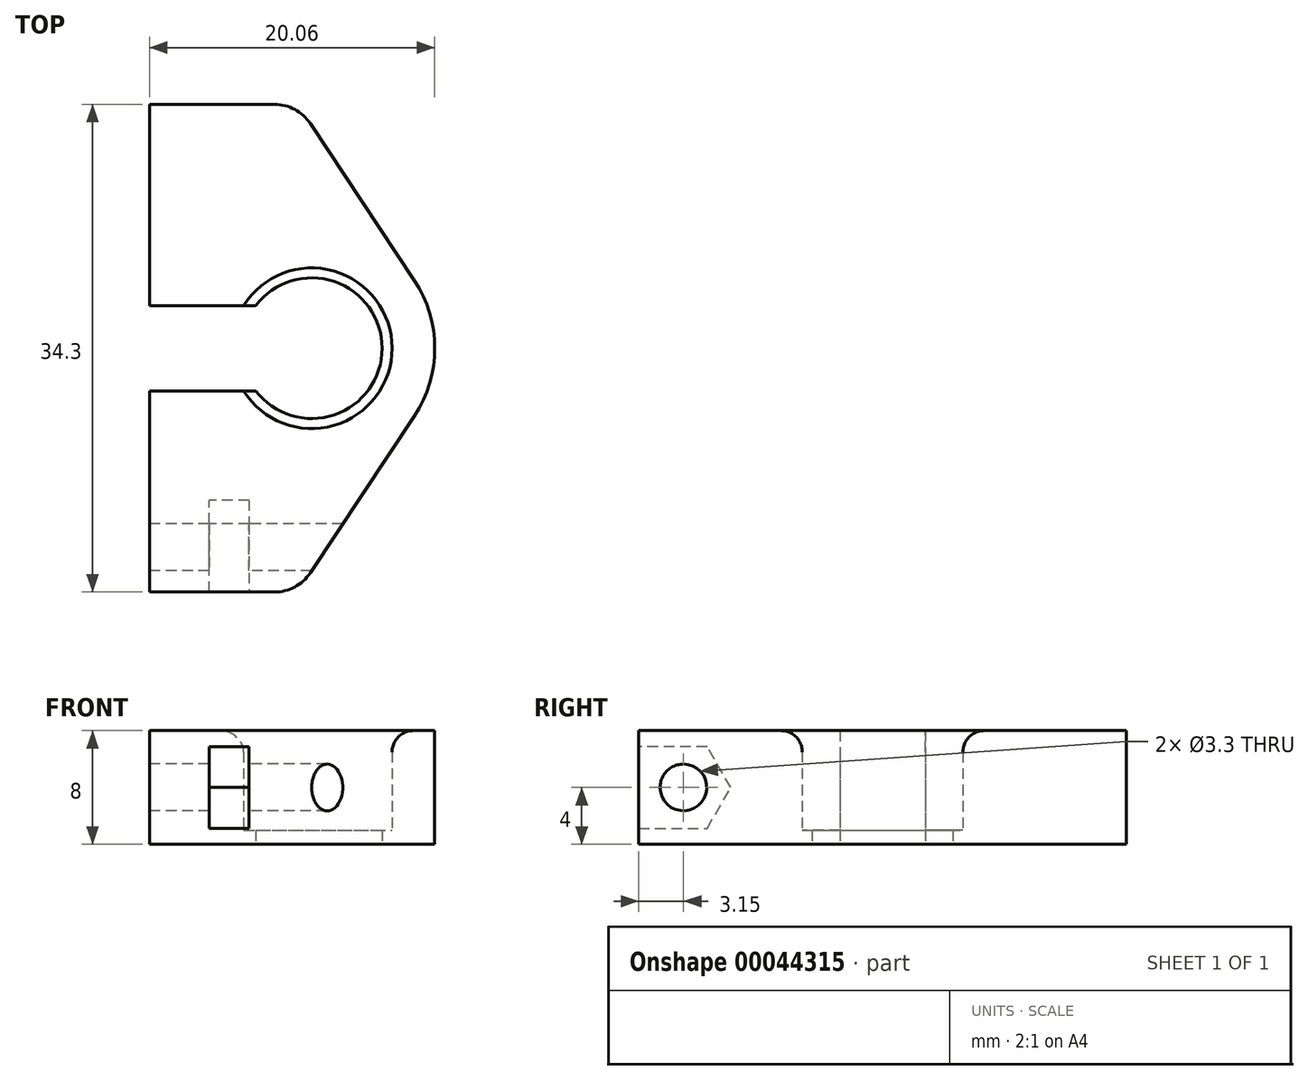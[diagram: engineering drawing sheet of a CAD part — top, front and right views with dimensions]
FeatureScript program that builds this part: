
annotation { "Feature Type Name" : "Feature", "Feature Type Description" : "" }
export const myFeature = defineFeature(function(context is Context, id is Id, definition is map)
    precondition{}
    {
        {
            assignVariable(context, id + "F0", {"name" : "Toleranz", "anyValue" : 0.3});
        }
        {
            assignVariable(context, id + "F1", {"name" : "BearingHeight", "anyValue" : 8});
        }
        {
            var Q0;
            Q0=qCreatedBy(makeId("Top.planeOp"),FACE);
            var sketch = newSketch(context, id + "F2", { "sketchPlane" : qUnion([Q0])});
            skCircle(sketch, "E0", {"center": v(0, 0) * mm, "radius": 2.65 * mm});
            skCircle(sketch, "E1", {"center": v(0, 0) * mm, "radius": 5.65 * mm});
            skCircle(sketch, "E2", {"center": v(0, 0) * mm, "radius": 8.65 * mm});
            skPoint(sketch, "E3", {"position": v(-11.4, 0) * mm});
            skLineSegment(sketch, "E4", {"start": v(-11.4, 3) * mm, "end": v(-11.4, -3) * mm, "construction": true});
            skLineSegment(sketch, "E5", {"start": v(-11.4, -17.15) * mm, "end": v(-1, -17.15) * mm});
            skLineSegment(sketch, "E6", {"start": v(-1, -17.15) * mm, "end": v(7.2, -4.78) * mm});
            skLineSegment(sketch, "E7", {"start": v(-11.4, 0) * mm, "end": v(-11.4, -17.15) * mm});
            skLineSegment(sketch, "E8", {"start": v(-28.2, 0) * mm, "end": v(26.8, 0) * mm, "construction": true});
            skLineSegment(sketch, "E9.MirrorCS", {"start": v(-1, 17.15) * mm, "end": v(7.2, 4.78) * mm});
            skLineSegment(sketch, "E10.MirrorCS", {"start": v(-11.4, 17.15) * mm, "end": v(-1, 17.15) * mm});
            skLineSegment(sketch, "E11.MirrorCS", {"start": v(-11.4, 0) * mm, "end": v(-11.41, 17.15) * mm});
            skCircle(sketch, "E12", {"center": v(0, 0) * mm, "radius": 4.95 * mm});
            skLineSegment(sketch, "E13", {"start": v(-11.4, -3) * mm, "end": v(-3.94, -3) * mm});
            skLineSegment(sketch, "E14.MirrorCS", {"start": v(-11.4, 3) * mm, "end": v(-3.94, 3) * mm});
            skSolve(sketch);
        }
        {
            var Q0;
            {var subQ2=sQuery(id+"F2.wireOp",EDGE,"3LThoHS6-l1Lm-BIrZ-PV6s-VWp7ep7WF0tf");Q0=makeQuery(id+"F2.imprint","IMPRINT",FACE,{"disambiguationData":[TD([[makeQuery(id+"F2.imprint","IMPRINT",EDGE,{"derivedFrom":subQ2}),-1.0]])]});}
            var Q1;
            {var subQ2=sQuery(id+"F2.wireOp",EDGE,"E9.MirrorCS");Q1=makeQuery(id+"F2.imprint","IMPRINT",FACE,{"disambiguationData":[TD([[makeQuery(id+"F2.imprint","IMPRINT",EDGE,{"derivedFrom":subQ2}),-1.0]])]});}
            var Q2;
            {var subQ1=sQuery(id+"F2.wireOp",EDGE,"E5");Q2=makeQuery(id+"F2.imprint","IMPRINT",FACE,{"disambiguationData":[TD([[makeQuery(id+"F2.imprint","IMPRINT",EDGE,{"derivedFrom":subQ1}),1.0]])]});}
            var Q3;
            {var subQ3=sQuery(id+"F2.wireOp",EDGE,"E13");var subQ7=sQuery(id+"F2.wireOp",EDGE,"E1");var subQ8=makeQuery(id+"F2.imprint","INTERSECT",VERTEX,{"derivedFrom":[subQ7,subQ3]});Q3=makeQuery(id+"F2.imprint","IMPRINT",FACE,{"disambiguationData":[TD([[makeQuery(id+"F2.imprint","IMPRINT",EDGE,{"disambiguationData":[TD([[subQ8,-1.0]])],"derivedFrom":subQ7}),-1.0]])]});}
            extrude(context, id + "F3", {"entities" : qUnion([Q0, Q1, Q2, Q3]), "depth" : (getVariable(context, 'BearingHeight')) * mm});
        }
        {
            var Q0;
            {var subQ0=sQuery(id+"F2.wireOp",EDGE,"E13");var subQ1=sQuery(id+"F2.wireOp",EDGE,"E1");var subQ2=makeQuery(id+"F2.imprint","INTERSECT",VERTEX,{"derivedFrom":[subQ1,subQ0]});Q0=makeQuery(id+"F2.imprint","IMPRINT",FACE,{"disambiguationData":[TD([[makeQuery(id+"F2.imprint","IMPRINT",EDGE,{"disambiguationData":[TD([[subQ2,-1.0]])],"derivedFrom":subQ1}),1.0]])]});}
            extrude(context, id + "F4", {"entities" : qUnion([Q0]), "operationType" : NewBodyOperationType.ADD, "depth" : 1 * mm});
        }
        {
            var Q0;
            Q0=makeQuery(id+"F3.opExtrude","SWEPT_FACE",FACE,{"disambiguationData":[OSD([sQuery(id+"F2.wireOp",EDGE,"E7")])]});
            var sketch = newSketch(context, id + "F5", { "sketchPlane" : qUnion([Q0])});
            skCircle(sketch, "E15", {"center": v(14, 4) * mm, "radius": 1.65 * mm});
            skPoint(sketch, "E16", {"position": v(3, 4) * mm});
            skCircle(sketch, "E17.cCircle", {"center": v(14, 4) * mm, "radius": 2.87 * mm, "construction": true});
            skLineSegment(sketch, "E17.0", {"start": v(17.32, 4) * mm, "end": v(15.66, 1.12) * mm});
            skLineSegment(sketch, "E17.1", {"start": v(15.66, 1.12) * mm, "end": v(12.34, 1.13) * mm});
            skLineSegment(sketch, "E17.2", {"start": v(12.34, 1.13) * mm, "end": v(10.68, 4) * mm});
            skLineSegment(sketch, "E17.3", {"start": v(10.68, 4) * mm, "end": v(12.34, 6.88) * mm});
            skLineSegment(sketch, "E17.4", {"start": v(12.34, 6.88) * mm, "end": v(15.66, 6.87) * mm});
            skLineSegment(sketch, "E17.5", {"start": v(15.66, 6.87) * mm, "end": v(17.32, 4) * mm});
            skPoint(sketch, "E17.0.midPoint", {"position": v(16.49, 2.56) * mm});
            skLineSegment(sketch, "E18", {"start": v(0, 0) * mm, "end": v(0, 8) * mm, "construction": true});
            skCircle(sketch, "E19.MirrorC", {"center": v(-14, 4) * mm, "radius": 1.65 * mm});
            skSolve(sketch);
        }
        {
            var Q0;
            Q0=makeQuery(id+"F5.imprint","IMPRINT",FACE,{"disambiguationData":[TD([[makeQuery(id+"F5.imprint","IMPRINT",EDGE,{"derivedFrom":sQuery(id+"F5.wireOp",EDGE,"E15")}),1.0]])]});
            var Q1;
            Q1=makeQuery(id+"F5.imprint","IMPRINT",FACE,{"disambiguationData":[TD([[makeQuery(id+"F5.imprint","IMPRINT",EDGE,{"derivedFrom":sQuery(id+"F5.wireOp",EDGE,"3b39c7fe-ee25-41de-868a-32cebd3cabf80.MirrorC")}),-1.0]])]});
            var Q2;
            Q2=makeQuery(id+"F5.imprint","IMPRINT",FACE,{"disambiguationData":[TD([[makeQuery(id+"F5.imprint","IMPRINT",EDGE,{"derivedFrom":sQuery(id+"F5.wireOp",EDGE,"E19.MirrorC")}),-1.0]])]});
            extrude(context, id + "F6", {"entities" : qUnion([Q0, Q1, Q2]), "operationType" : NewBodyOperationType.REMOVE, "endBound" : BoundingType.UP_TO_NEXT, "oppositeDirection" : true, "depth" : 25 * mm});
        }
        {
            var Q0;
            Q0=makeQuery(id+"F3.opExtrude","SWEPT_FACE",FACE,{"disambiguationData":[OSD([sQuery(id+"F2.wireOp",EDGE,"E7")])]});
            cPlane(context, id + "F7", {"entities" : qUnion([Q0]), "cplaneType" : CPlaneType.OFFSET, "offset" : 4.2 * mm, "oppositeDirection" : true, "width" : 150 * mm, "height" : 150 * mm});
        }
        {
            var Q0;
            Q0=qCreatedBy(id+"F7.planeOp",FACE);
            var sketch = newSketch(context, id + "F8", { "sketchPlane" : qUnion([Q0])});
            skLineSegment(sketch, "E20.0", {"start": v(15.66, 6.87) * mm, "end": v(17.32, 4) * mm});
            skLineSegment(sketch, "E21.0", {"start": v(12.34, 6.88) * mm, "end": v(15.66, 6.87) * mm});
            skLineSegment(sketch, "E22.0", {"start": v(10.68, 4) * mm, "end": v(12.34, 6.88) * mm});
            skLineSegment(sketch, "E23.0", {"start": v(12.34, 1.13) * mm, "end": v(10.68, 4) * mm});
            skLineSegment(sketch, "E24.0", {"start": v(15.66, 1.12) * mm, "end": v(12.34, 1.13) * mm});
            skLineSegment(sketch, "E25.0", {"start": v(17.32, 4) * mm, "end": v(15.66, 1.12) * mm});
            skLineSegment(sketch, "E26.0.0", {"start": v(3, 8) * mm, "end": v(3, 0) * mm, "construction": true});
            skLineSegment(sketch, "E26.0.1", {"start": v(3, 0) * mm, "end": v(17.15, 0) * mm, "construction": true});
            skLineSegment(sketch, "E26.0.2", {"start": v(17.15, 0) * mm, "end": v(17.15, 8) * mm, "construction": true});
            skLineSegment(sketch, "E26.0.3", {"start": v(17.15, 8) * mm, "end": v(3, 8) * mm, "construction": true});
            skLineSegment(sketch, "E27", {"start": v(15.66, 6.87) * mm, "end": v(17.15, 6.87) * mm});
            skPoint(sketch, "E27.endSnap0", {"position": v(17.15, 4) * mm});
            skLineSegment(sketch, "E28", {"start": v(17.15, 6.87) * mm, "end": v(17.15, 1.12) * mm});
            skLineSegment(sketch, "E29", {"start": v(17.15, 1.12) * mm, "end": v(15.66, 1.12) * mm});
            skSolve(sketch);
        }
        {
            var Q0;
            Q0 = qSketchRegion(id + "F8", true);
            extrude(context, id + "F9", {"entities" : qUnion([Q0]), "operationType" : NewBodyOperationType.REMOVE, "oppositeDirection" : true, "depth" : (2.5 + getVariable(context, 'Toleranz')) * mm});
        }
        {
            var Q0;
            Q0=makeQuery(id+"F3.opExtrude","CAP_EDGE",EDGE,{"disambiguationData":[OSD([sQuery(id+"F2.wireOp",EDGE,"E1")])],"isStart":false});
            fillet(context, id + "F10", {"entities" : qUnion([Q0]), "radius" : 1.5 * mm, "tangentPropagation" : true, "allowEdgeOverflow" : false});
        }
        {
            var Q0;
            Q0=makeQuery(id+"F3.opExtrude","SWEPT_EDGE",EDGE,{"disambiguationData":[OSD([sQuery(id+"F2.wireOp",EDGE,"E5"),sQuery(id+"F2.wireOp",EDGE,"E6")])]});
            var Q1;
            Q1=makeQuery(id+"F3.opExtrude","SWEPT_EDGE",EDGE,{"disambiguationData":[OSD([sQuery(id+"F2.wireOp",EDGE,"E9.MirrorCS"),sQuery(id+"F2.wireOp",EDGE,"E10.MirrorCS")])]});
            fillet(context, id + "F11", {"entities" : qUnion([Q0, Q1]), "radius" : 3 * mm, "tangentPropagation" : true, "allowEdgeOverflow" : false});
        }
    });
